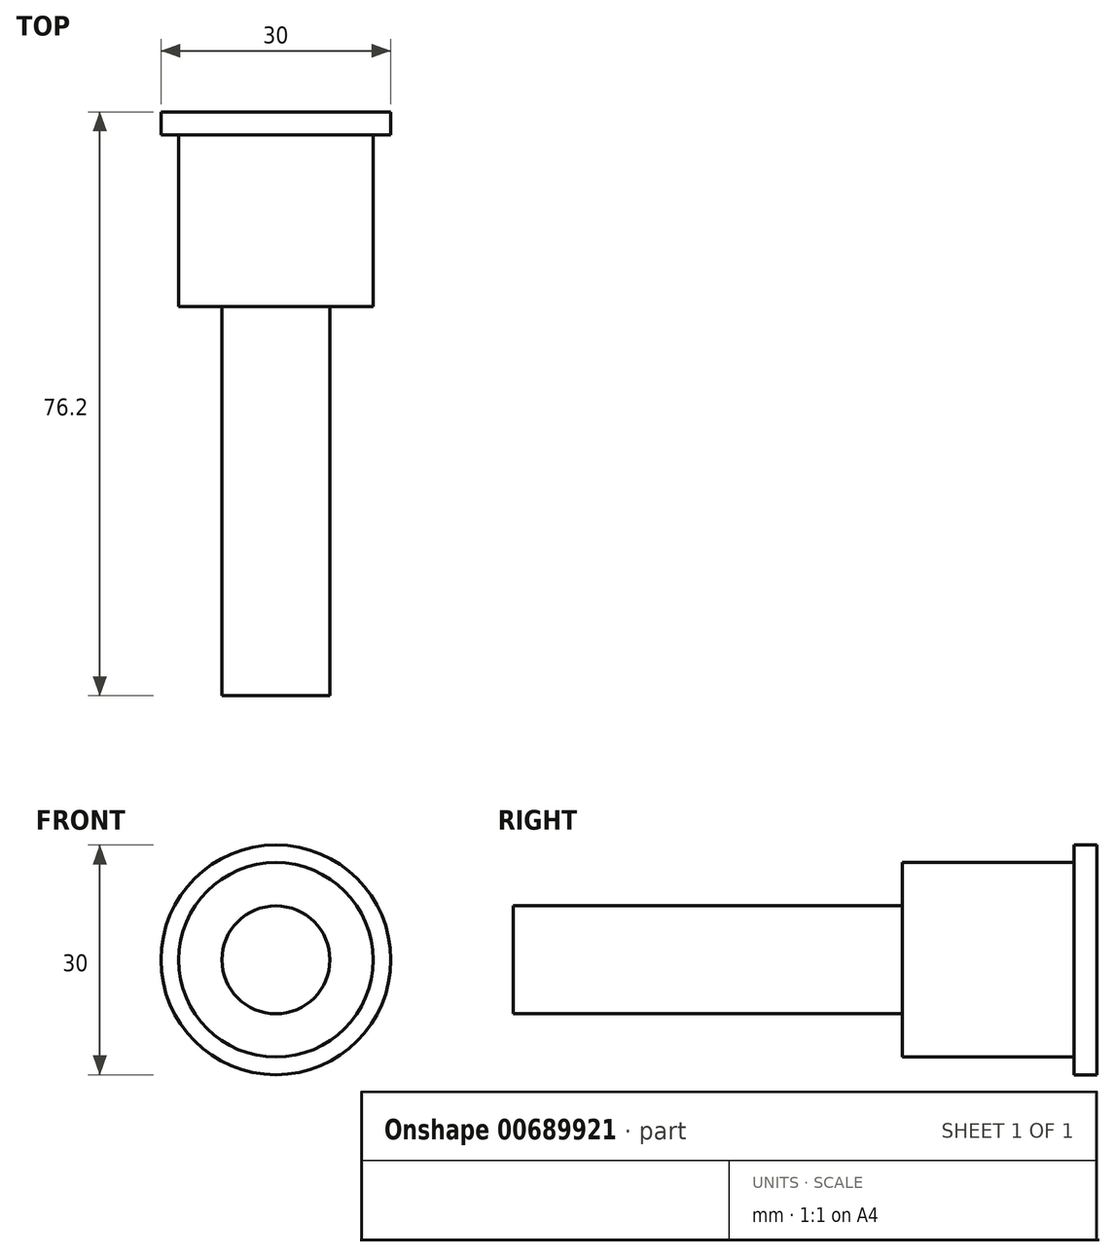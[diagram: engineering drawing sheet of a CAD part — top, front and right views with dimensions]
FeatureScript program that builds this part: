
annotation { "Feature Type Name" : "Feature", "Feature Type Description" : "" }
export const myFeature = defineFeature(function(context is Context, id is Id, definition is map)
    precondition{}
    {
        {
            var Q0;
            Q0=qCreatedBy(makeId("Front.planeOp"),FACE);
            var sketch = newSketch(context, id + "F0", { "sketchPlane" : qUnion([Q0])});
            skCircle(sketch, "E0", {"center": v(0, 0) * mm, "radius": 7.05 * mm});
            skSolve(sketch);
        }
        {
            var Q0;
            Q0=makeQuery(id+"F0.imprint","IMPRINT",FACE,{"disambiguationData":[TD([[makeQuery(id+"F0.imprint","IMPRINT",EDGE,{"derivedFrom":sQuery(id+"F0.wireOp",EDGE,"E0")}),1.0]])]});
            extrude(context, id + "F1", {"entities" : qUnion([Q0]), "depth" : 50.8 * mm, "offsetDistance" : 25 * mm});
        }
        {
            var Q0;
            Q0=qCreatedBy(makeId("Front.planeOp"),FACE);
            var sketch = newSketch(context, id + "F2", { "sketchPlane" : qUnion([Q0])});
            skCircle(sketch, "E1", {"center": v(0, 0) * mm, "radius": 12.7 * mm});
            skSolve(sketch);
        }
        {
            var Q0;
            Q0 = qSketchRegion(id + "F2", true);
            extrude(context, id + "F3", {"entities" : qUnion([Q0]), "operationType" : NewBodyOperationType.ADD, "oppositeDirection" : true, "depth" : 25.4 * mm, "offsetDistance" : 25 * mm});
        }
        {
            var Q0;
            Q0=makeQuery(id+"F3.opExtrude","CAP_FACE",FACE,{"disambiguationData":[OSD([sQuery(id+"F2.wireOp",EDGE,"E1")])],"isStart":false});
            var sketch = newSketch(context, id + "F4", { "sketchPlane" : qUnion([Q0])});
            skCircle(sketch, "E2", {"center": v(0, 0) * mm, "radius": 15 * mm});
            skSolve(sketch);
        }
        {
            var Q0;
            Q0 = qSketchRegion(id + "F4", true);
            extrude(context, id + "F5", {"entities" : qUnion([Q0]), "operationType" : NewBodyOperationType.ADD, "oppositeDirection" : true, "depth" : 3 * mm, "offsetDistance" : 25 * mm});
        }
    });
